# Revit family: Shower-Handshower_Kit-KALLISTA-Bellis-P24653-2
name_source: partatom
category: Plumbing Fixtures
units: mm (PartAtom-declared; Revit-internal decimal feet)

## family parameters
Cut with Voids When Loaded = No
Host = Face
Maintain Annotation Orientation = No
OmniClass Number = 23.31.17.00
Part Type = Normal
Room Calculation Point = No
Round Connector Dimension = Use Diameter
Shared = No

## types (5) — shared parameters
ADA Compliant = No
Assembly Code = D2010700
CW Connection = No
Cold Water Inlet = Cold Water Inlet
Date Modified = 05/28/2025
Default Elevation = 42"
Description = Single-function Handshower and Hose with 1.75 GPM
Drain Included = No
Flow Rate = 2 GPM
HW Connection = Yes
Height = 10 15/16"
Hot Water Inlet = Hot Water Inlet
Length = 2 7/8"
Manufacturer = Kallista Co.
Master Format 2014 = 22 42 23
Master Format 2014 Name = Residential Showers
Material = Premium Metal Construction
Pressure = 80.00 psi
Product Documentation Link = https://techcomm.kohler.com
Product Name = Bellis
Tempered Water Inlet = Tempered Water Inlet
URL = https://www.kallista.com
Vent Connection = No
Waste Connection = No
Waste Water Outlet = Waste Water Outlet
WaterSense Certified = Yes
Width = 3"

## per-type parameters (varying)
| type | Finish | Model | Product Page URL | Type |
| 2MB-Brushed Brass | Kallista-Metal-2MB-Brushed_Brass | P24653-00-2MB |  | 1 |
| AD-Nickel Silver | Kallista-Metal-AD-Nickel_Silver | P24653-00-AD | https://www.kallista.com | 2 |
| AG-Brushed Nickel | Kallista-Metal-AG-Brushed_Nickel | P24653-00-AG |  | 3 |
| CP-Chrome | Kallista-Metal-CP-Chrome | P24653-00-CP | https://www.kallista.com | 4 |
| ULB-Unlaquered Brass | Kallista-Metal-ULB-Unlaquered_Brass | P24653-00-ULB | https://www.kallista.com | 5 |

## geometry (parser evidence)
native form markers: Sweep x4
no freeform markers — native parametric forms only
